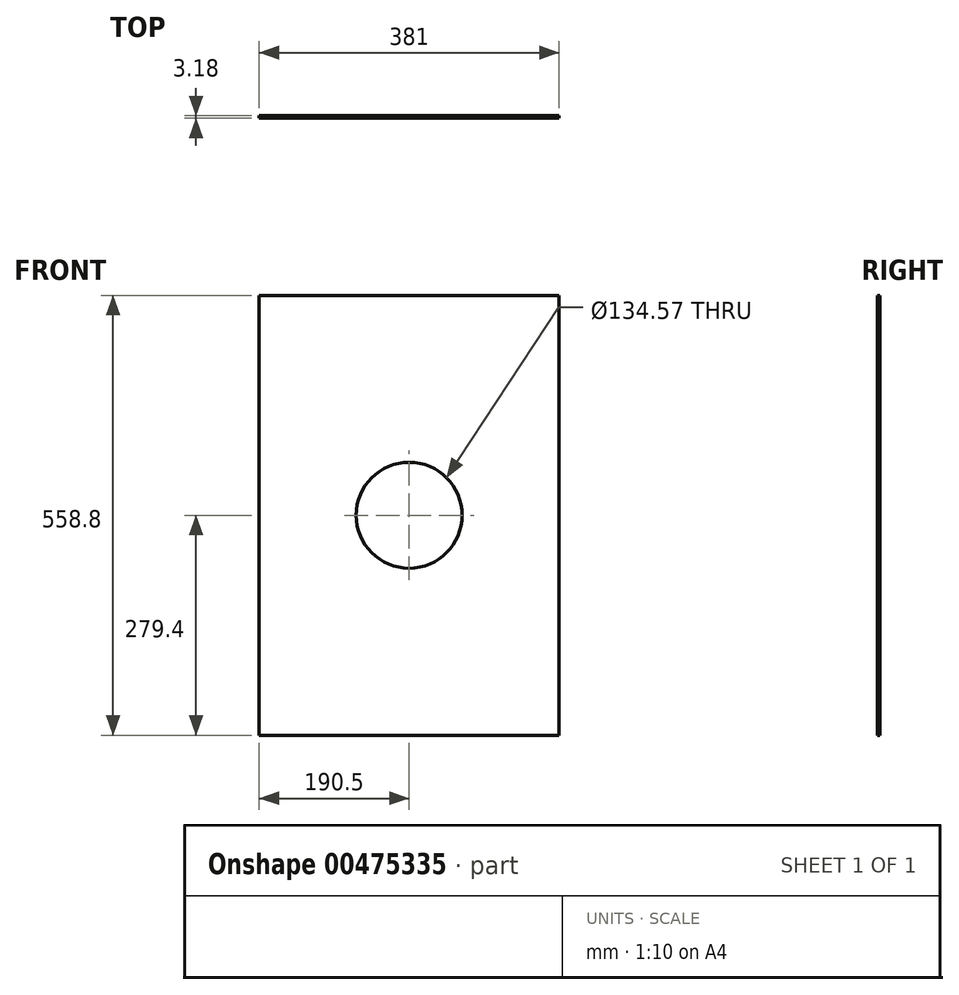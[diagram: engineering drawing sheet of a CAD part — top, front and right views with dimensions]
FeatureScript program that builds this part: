
annotation { "Feature Type Name" : "Feature", "Feature Type Description" : "" }
export const myFeature = defineFeature(function(context is Context, id is Id, definition is map)
    precondition{}
    {
        {
            var Q0;
            Q0=qCreatedBy(makeId("Front.planeOp"),FACE);
            var sketch = newSketch(context, id + "F0", { "sketchPlane" : qUnion([Q0])});
            skCircle(sketch, "E0", {"center": v(0, 0) * mm, "radius": 67.28 * mm});
            skLineSegment(sketch, "E1", {"start": v(-190.5, 0) * mm, "end": v(-190.5, 279.4) * mm});
            skLineSegment(sketch, "E2", {"start": v(-190.5, 0) * mm, "end": v(-190.5, -279.4) * mm});
            skLineSegment(sketch, "E3", {"start": v(-190.5, -279.4) * mm, "end": v(190.5, -279.4) * mm});
            skLineSegment(sketch, "E4", {"start": v(-190.5, 279.4) * mm, "end": v(190.5, 279.4) * mm});
            skLineSegment(sketch, "E5", {"start": v(190.5, -279.4) * mm, "end": v(190.5, 279.4) * mm});
            skSolve(sketch);
        }
        {
            var Q0;
            Q0 = qSketchRegion(id + "F0", true);
            extrude(context, id + "F1", {"entities" : qUnion([Q0]), "depth" : 3.17 * mm});
        }
    });
